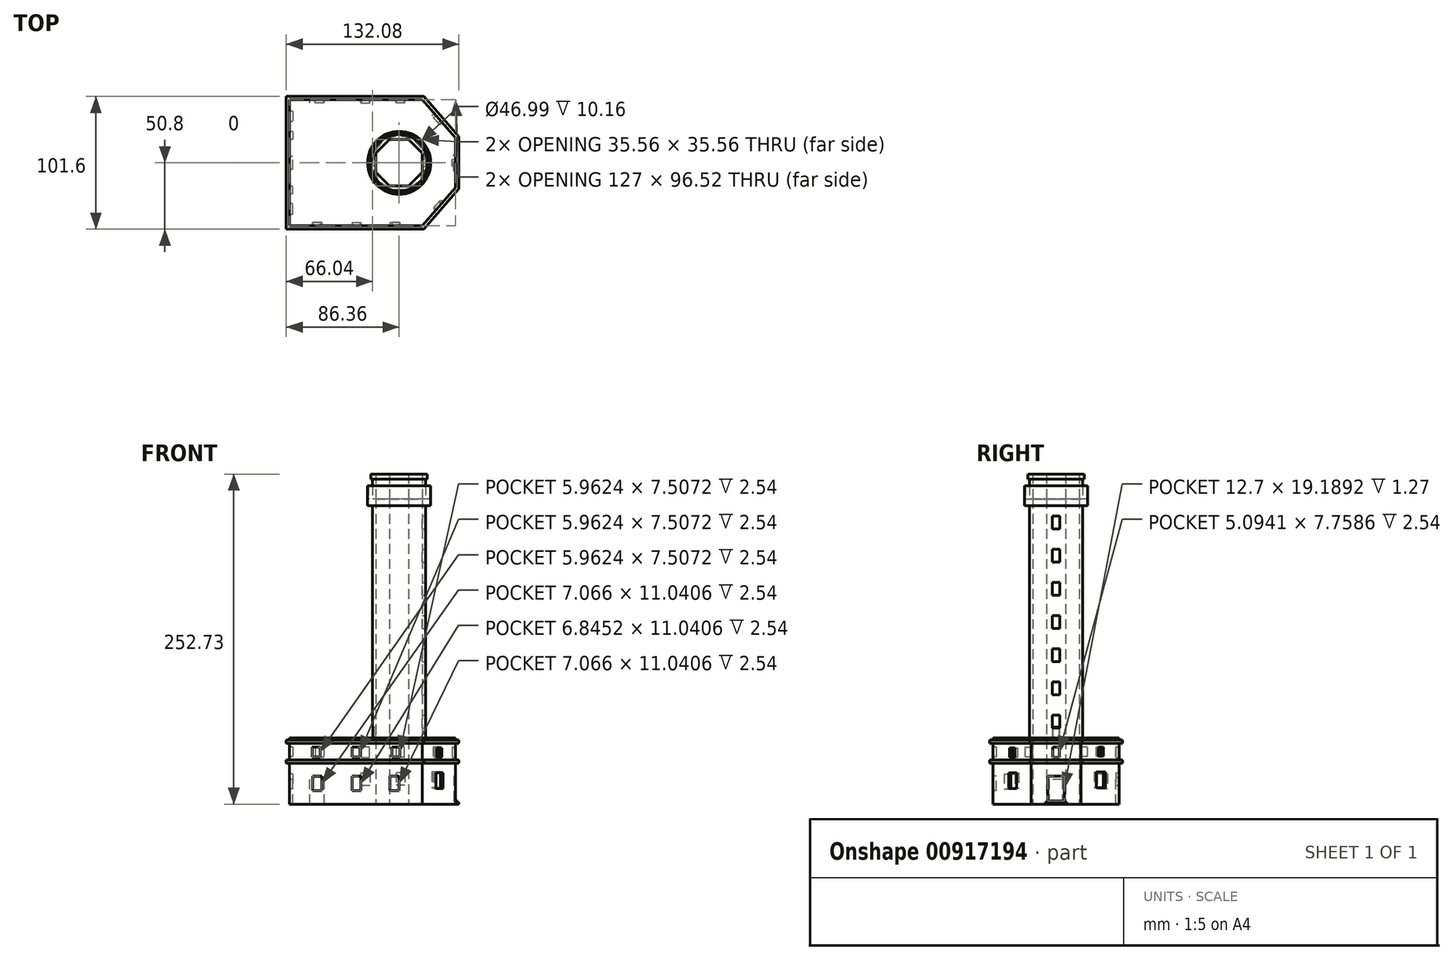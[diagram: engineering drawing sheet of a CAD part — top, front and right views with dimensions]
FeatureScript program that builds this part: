
annotation { "Feature Type Name" : "Feature", "Feature Type Description" : "" }
export const myFeature = defineFeature(function(context is Context, id is Id, definition is map)
    precondition{}
    {
        {
            var Q0;
            Q0=qCreatedBy(makeId("Top.planeOp"),FACE);
            var sketch = newSketch(context, id + "F0", { "sketchPlane" : qUnion([Q0])});
            skLineSegment(sketch, "E0.bottom", {"start": v(50.8, -48.26) * mm, "end": v(-50.8, -48.26) * mm});
            skLineSegment(sketch, "E0.top", {"start": v(50.8, 48.26) * mm, "end": v(-50.8, 48.26) * mm});
            skLineSegment(sketch, "E0.right", {"start": v(-50.8, -48.26) * mm, "end": v(-50.8, 48.26) * mm});
            skPoint(sketch, "E0.middle", {"position": v(0, 0) * mm});
            skLineSegment(sketch, "E1.left", {"start": v(76.2, -19.05) * mm, "end": v(76.2, 19.05) * mm});
            skPoint(sketch, "E1.middle", {"position": v(50.8, 0) * mm});
            skLineSegment(sketch, "E2", {"start": v(50.8, 48.26) * mm, "end": v(76.2, 19.05) * mm});
            skLineSegment(sketch, "E3", {"start": v(50.8, -48.26) * mm, "end": v(76.2, -19.05) * mm});
            skSolve(sketch);
        }
        {
            var Q0;
            Q0=makeQuery(id+"F0.imprint","IMPRINT",FACE,{"disambiguationData":[TD([[makeQuery(id+"F0.imprint","IMPRINT",EDGE,{"derivedFrom":sQuery(id+"F0.wireOp",EDGE,"E0.bottom")}),-1.0]])]});
            extrude(context, id + "F1", {"entities" : qUnion([Q0]), "depth" : 50.8 * mm, "offsetDistance" : 25.4 * mm});
        }
        {
            var Q0;
            Q0=makeQuery(id+"F1.opExtrude","CAP_FACE",FACE,{"disambiguationData":[OSD([sQuery(id+"F0.wireOp",EDGE,"E0.bottom"),sQuery(id+"F0.wireOp",EDGE,"E0.top"),sQuery(id+"F0.wireOp",EDGE,"E0.right"),sQuery(id+"F0.wireOp",EDGE,"E1.left"),sQuery(id+"F0.wireOp",EDGE,"E2"),sQuery(id+"F0.wireOp",EDGE,"E3")])],"isStart":false});
            var sketch = newSketch(context, id + "F2", { "sketchPlane" : qUnion([Q0])});
            skCircle(sketch, "E4", {"center": v(33.02, 0) * mm, "radius": 20.32 * mm});
            skSolve(sketch);
        }
        {
            var Q0;
            Q0=makeQuery(id+"F2.imprint","IMPRINT",FACE,{"disambiguationData":[TD([[makeQuery(id+"F2.imprint","IMPRINT",EDGE,{"derivedFrom":sQuery(id+"F2.wireOp",EDGE,"E4")}),1.0]])]});
            extrude(context, id + "F3", {"entities" : qUnion([Q0]), "operationType" : NewBodyOperationType.ADD, "depth" : 177.8 * mm, "offsetDistance" : 25.4 * mm});
        }
        {
            var Q0;
            Q0=qCreatedBy(makeId("Top.planeOp"),FACE);
            var sketch = newSketch(context, id + "F4", { "sketchPlane" : qUnion([Q0])});
            skCircle(sketch, "E5.0", {"center": v(33.02, 0) * mm, "radius": 20.32 * mm});
            skPoint(sketch, "E6.0.midPoint", {"position": v(45.32, -7.29) * mm});
            skLineSegment(sketch, "E7", {"start": v(33.02, 0) * mm, "end": v(50.8, 0) * mm});
            skCircle(sketch, "E8.cCircle", {"center": v(33.02, 0) * mm, "radius": 17.78 * mm, "construction": true});
            skLineSegment(sketch, "E8.0", {"start": v(50.8, 7.36) * mm, "end": v(50.8, -7.36) * mm});
            skLineSegment(sketch, "E8.1", {"start": v(50.8, -7.36) * mm, "end": v(40.38, -17.78) * mm});
            skLineSegment(sketch, "E8.2", {"start": v(40.38, -17.78) * mm, "end": v(25.66, -17.78) * mm});
            skLineSegment(sketch, "E8.3", {"start": v(25.66, -17.78) * mm, "end": v(15.24, -7.36) * mm});
            skLineSegment(sketch, "E8.4", {"start": v(15.24, -7.36) * mm, "end": v(15.24, 7.36) * mm});
            skLineSegment(sketch, "E8.5", {"start": v(15.24, 7.36) * mm, "end": v(25.66, 17.78) * mm});
            skLineSegment(sketch, "E8.6", {"start": v(25.66, 17.78) * mm, "end": v(40.38, 17.78) * mm});
            skLineSegment(sketch, "E8.7", {"start": v(40.38, 17.78) * mm, "end": v(50.8, 7.36) * mm});
            skPoint(sketch, "E8.0.midPoint", {"position": v(50.8, 0) * mm});
            skSolve(sketch);
        }
        {
            var Q0;
            {var subQ0=sQuery(id+"F4.wireOp",EDGE,"E8.0");var subQ1=makeQuery(id+"F4.imprint","IMPRINT",VERTEX,{"derivedFrom":subQ0});Q0=makeQuery(id+"F4.imprint","IMPRINT",FACE,{"disambiguationData":[TD([[makeQuery(id+"F4.imprint","IMPRINT",EDGE,{"disambiguationData":[TD([[subQ1,1.0]])],"derivedFrom":subQ0}),-1.0]])]});}
            extrude(context, id + "F5", {"entities" : qUnion([Q0]), "operationType" : NewBodyOperationType.REMOVE, "depth" : 381 * mm, "offsetDistance" : 25.4 * mm});
        }
        {
            var Q0;
            Q0=makeQuery(id+"F1.opExtrude","SWEPT_FACE",FACE,{"disambiguationData":[OSD([sQuery(id+"F0.wireOp",EDGE,"E0.top")])]});
            var sketch = newSketch(context, id + "F6", { "sketchPlane" : qUnion([Q0])});
            skLineSegment(sketch, "E9", {"start": v(-50.8, 50.8) * mm, "end": v(-50.8, 49.28) * mm});
            skLineSegment(sketch, "E10.bottom", {"start": v(-50.8, 49.28) * mm, "end": v(50.8, 49.28) * mm});
            skLineSegment(sketch, "E10.top", {"start": v(-50.8, 46.74) * mm, "end": v(50.8, 46.74) * mm});
            skLineSegment(sketch, "E10.left", {"start": v(-50.8, 49.28) * mm, "end": v(-50.8, 46.74) * mm});
            skLineSegment(sketch, "E10.right", {"start": v(50.8, 49.28) * mm, "end": v(50.8, 46.74) * mm});
            skLineSegment(sketch, "E11", {"start": v(-50.8, 46.74) * mm, "end": v(-50.8, 34.04) * mm});
            skLineSegment(sketch, "E12.bottom", {"start": v(-50.8, 34.04) * mm, "end": v(50.8, 34.04) * mm});
            skLineSegment(sketch, "E12.top", {"start": v(-50.8, 31.5) * mm, "end": v(50.8, 31.5) * mm});
            skLineSegment(sketch, "E12.left", {"start": v(-50.8, 34.04) * mm, "end": v(-50.8, 31.5) * mm});
            skLineSegment(sketch, "E12.right", {"start": v(50.8, 34.04) * mm, "end": v(50.8, 31.5) * mm});
            skLineSegment(sketch, "E13", {"start": v(-50.8, 40.39) * mm, "end": v(50.8, 40.39) * mm});
            skLineSegment(sketch, "E14", {"start": v(0, 50.8) * mm, "end": v(0, 31.5) * mm, "construction": true});
            skLineSegment(sketch, "E15.bottom", {"start": v(3.03, 35.7) * mm, "end": v(-3.03, 35.7) * mm});
            skLineSegment(sketch, "E15.top", {"start": v(3.03, 45.07) * mm, "end": v(-3.03, 45.07) * mm});
            skLineSegment(sketch, "E15.left", {"start": v(3.03, 35.7) * mm, "end": v(3.03, 45.07) * mm});
            skLineSegment(sketch, "E15.right", {"start": v(-3.03, 35.7) * mm, "end": v(-3.03, 45.07) * mm});
            skPoint(sketch, "E15.middle", {"position": v(0, 40.39) * mm});
            skLineSegment(sketch, "E16.1.0.0", {"start": v(30.48, 50.8) * mm, "end": v(30.48, 31.5) * mm, "construction": true});
            skLineSegment(sketch, "E16.2.0.0", {"start": v(60.96, 50.8) * mm, "end": v(60.96, 31.5) * mm, "construction": true});
            skLineSegment(sketch, "E16.direction1", {"start": v(0, 31.5) * mm, "end": v(30.48, 31.5) * mm, "construction": true});
            skLineSegment(sketch, "E17.1.0.0", {"start": v(-30.48, 50.8) * mm, "end": v(-30.48, 31.5) * mm, "construction": true});
            skPoint(sketch, "E17.1.0.1", {"position": v(-30.48, 40.39) * mm});
            skLineSegment(sketch, "E17.2.0.0", {"start": v(-60.96, 50.8) * mm, "end": v(-60.96, 31.5) * mm, "construction": true});
            skPoint(sketch, "E17.2.0.1", {"position": v(-60.96, 40.39) * mm});
            skLineSegment(sketch, "E17.direction1", {"start": v(0, 31.5) * mm, "end": v(-30.48, 31.5) * mm, "construction": true});
            skLineSegment(sketch, "E18.bottom", {"start": v(-27.7, 35.38) * mm, "end": v(-33.27, 35.38) * mm});
            skLineSegment(sketch, "E18.top", {"start": v(-27.7, 45.39) * mm, "end": v(-33.27, 45.39) * mm});
            skLineSegment(sketch, "E18.left", {"start": v(-27.7, 35.38) * mm, "end": v(-27.7, 45.39) * mm});
            skLineSegment(sketch, "E18.right", {"start": v(-33.27, 35.38) * mm, "end": v(-33.27, 45.39) * mm});
            skLineSegment(sketch, "E19.MirrorCS", {"start": v(27.7, 35.38) * mm, "end": v(27.7, 45.39) * mm});
            skLineSegment(sketch, "E20.MirrorCS", {"start": v(27.7, 35.38) * mm, "end": v(33.27, 35.38) * mm});
            skLineSegment(sketch, "E21.MirrorCS", {"start": v(33.27, 35.38) * mm, "end": v(33.27, 45.39) * mm});
            skLineSegment(sketch, "E22.MirrorCS", {"start": v(27.7, 45.39) * mm, "end": v(33.27, 45.39) * mm});
            skSolve(sketch);
        }
        {
            var Q0;
            Q0=makeQuery(id+"F6.imprint","IMPRINT",FACE,{"disambiguationData":[TD([[makeQuery(id+"F6.imprint","IMPRINT",EDGE,{"derivedFrom":sQuery(id+"F6.wireOp",EDGE,"E10.bottom")}),-1.0]])]});
            var Q1;
            Q1=makeQuery(id+"F6.imprint","IMPRINT",FACE,{"disambiguationData":[TD([[makeQuery(id+"F6.imprint","IMPRINT",EDGE,{"derivedFrom":sQuery(id+"F6.wireOp",EDGE,"E12.bottom")}),-1.0]])]});
            extrude(context, id + "F7", {"entities" : qUnion([Q0, Q1]), "operationType" : NewBodyOperationType.ADD, "depth" : 2.54 * mm, "offsetDistance" : 25.4 * mm});
        }
        {
            var Q0;
            Q0=makeQuery(id+"F1.opExtrude","SWEPT_FACE",FACE,{"disambiguationData":[OSD([sQuery(id+"F0.wireOp",EDGE,"E2")])]});
            var sketch = newSketch(context, id + "F8", { "sketchPlane" : qUnion([Q0])});
            skLineSegment(sketch, "E23", {"start": v(-35.63, 50.8) * mm, "end": v(-35.63, 49.28) * mm});
            skLineSegment(sketch, "E24.bottom", {"start": v(-35.63, 49.28) * mm, "end": v(3.08, 49.28) * mm});
            skLineSegment(sketch, "E24.top", {"start": v(-35.63, 46.74) * mm, "end": v(3.08, 46.74) * mm});
            skLineSegment(sketch, "E24.left", {"start": v(-35.63, 49.28) * mm, "end": v(-35.63, 46.74) * mm});
            skLineSegment(sketch, "E24.right", {"start": v(3.08, 49.28) * mm, "end": v(3.08, 46.74) * mm});
            skLineSegment(sketch, "E25.bottom", {"start": v(3.08, 34.04) * mm, "end": v(-35.63, 34.04) * mm});
            skLineSegment(sketch, "E25.top", {"start": v(3.08, 31.5) * mm, "end": v(-35.63, 31.5) * mm});
            skLineSegment(sketch, "E25.left", {"start": v(3.08, 34.04) * mm, "end": v(3.08, 31.5) * mm});
            skLineSegment(sketch, "E25.right", {"start": v(-35.63, 34.04) * mm, "end": v(-35.63, 31.5) * mm});
            skSolve(sketch);
        }
        {
            var Q0;
            Q0=makeQuery(id+"F8.imprint","IMPRINT",FACE,{"disambiguationData":[TD([[makeQuery(id+"F8.imprint","IMPRINT",EDGE,{"derivedFrom":sQuery(id+"F8.wireOp",EDGE,"E24.bottom")}),-1.0]])]});
            var Q1;
            Q1=makeQuery(id+"F8.imprint","IMPRINT",FACE,{"disambiguationData":[TD([[makeQuery(id+"F8.imprint","IMPRINT",EDGE,{"derivedFrom":sQuery(id+"F8.wireOp",EDGE,"E25.bottom")}),1.0]])]});
            extrude(context, id + "F9", {"entities" : qUnion([Q0, Q1]), "operationType" : NewBodyOperationType.ADD, "depth" : 2.54 * mm, "offsetDistance" : 25.4 * mm});
        }
        {
            var Q0;
            Q0=makeQuery(id+"F7.opExtrude","SWEPT_FACE",FACE,{"disambiguationData":[OSD([sQuery(id+"F6.wireOp",EDGE,"E10.left")])]});
            extrude(context, id + "F10", {"entities" : qUnion([Q0]), "operationType" : NewBodyOperationType.ADD, "depth" : 1.14 * mm, "offsetDistance" : 25.4 * mm});
        }
        {
            var Q0;
            Q0=makeQuery(id+"F9.opExtrude","SWEPT_FACE",FACE,{"disambiguationData":[OSD([sQuery(id+"F8.wireOp",EDGE,"E24.right")])]});
            extrude(context, id + "F11", {"entities" : qUnion([Q0]), "operationType" : NewBodyOperationType.ADD, "depth" : 1.14 * mm, "offsetDistance" : 25.4 * mm});
        }
        {
            var Q0;
            Q0=makeQuery(id+"F7.opExtrude","SWEPT_FACE",FACE,{"disambiguationData":[OSD([sQuery(id+"F6.wireOp",EDGE,"E12.left")])]});
            extrude(context, id + "F12", {"entities" : qUnion([Q0]), "operationType" : NewBodyOperationType.ADD, "depth" : 1.14 * mm, "offsetDistance" : 25.4 * mm});
        }
        {
            var Q0;
            Q0=makeQuery(id+"F9.opExtrude","SWEPT_FACE",FACE,{"disambiguationData":[OSD([sQuery(id+"F8.wireOp",EDGE,"E25.left")])]});
            extrude(context, id + "F13", {"entities" : qUnion([Q0]), "operationType" : NewBodyOperationType.ADD, "depth" : 1.14 * mm, "offsetDistance" : 25.4 * mm});
        }
        {
            var Q0;
            Q0=makeQuery(id+"F1.opExtrude","SWEPT_FACE",FACE,{"disambiguationData":[OSD([sQuery(id+"F0.wireOp",EDGE,"E1.left")])]});
            var sketch = newSketch(context, id + "F14", { "sketchPlane" : qUnion([Q0])});
            skLineSegment(sketch, "E26.bottom", {"start": v(19.05, 49.28) * mm, "end": v(-19.05, 49.28) * mm});
            skLineSegment(sketch, "E26.top", {"start": v(19.05, 46.74) * mm, "end": v(-19.05, 46.74) * mm});
            skLineSegment(sketch, "E26.left", {"start": v(19.05, 49.28) * mm, "end": v(19.05, 46.74) * mm});
            skLineSegment(sketch, "E26.right", {"start": v(-19.05, 49.28) * mm, "end": v(-19.05, 46.74) * mm});
            skLineSegment(sketch, "E27.bottom", {"start": v(19.05, 34.04) * mm, "end": v(-19.05, 34.04) * mm});
            skLineSegment(sketch, "E27.top", {"start": v(19.05, 31.5) * mm, "end": v(-19.05, 31.5) * mm});
            skLineSegment(sketch, "E27.left", {"start": v(19.05, 34.04) * mm, "end": v(19.05, 31.5) * mm});
            skLineSegment(sketch, "E27.right", {"start": v(-19.05, 34.04) * mm, "end": v(-19.05, 31.5) * mm});
            skPoint(sketch, "E28.top.end.orphan", {"position": v(6.35, 21.6) * mm});
            skPoint(sketch, "E28.top.start.orphan", {"position": v(0, 21.6) * mm});
            skPoint(sketch, "E29.MirrorCS.end.orphan", {"position": v(-6.35, 21.6) * mm});
            skPoint(sketch, "E30.MirrorCS.end.orphan", {"position": v(-6.35, 21.59) * mm});
            skPoint(sketch, "E30.MirrorCS.start.orphan", {"position": v(-6.35, 0) * mm});
            skPoint(sketch, "E28.bottom.end.orphan", {"position": v(6.35, 0) * mm});
            skPoint(sketch, "E28.bottom.start.orphan", {"position": v(0, 0) * mm});
            skSolve(sketch);
        }
        {
            var Q0;
            Q0=makeQuery(id+"F14.imprint","IMPRINT",FACE,{"disambiguationData":[TD([[makeQuery(id+"F14.imprint","IMPRINT",EDGE,{"derivedFrom":sQuery(id+"F14.wireOp",EDGE,"E26.bottom")}),1.0]])]});
            var Q1;
            Q1=makeQuery(id+"F14.imprint","IMPRINT",FACE,{"disambiguationData":[TD([[makeQuery(id+"F14.imprint","IMPRINT",EDGE,{"derivedFrom":sQuery(id+"F14.wireOp",EDGE,"E27.bottom")}),1.0]])]});
            extrude(context, id + "F15", {"entities" : qUnion([Q0, Q1]), "operationType" : NewBodyOperationType.ADD, "depth" : 2.54 * mm, "offsetDistance" : 25.4 * mm});
        }
        {
            var Q0;
            Q0=makeQuery(id+"F15.opExtrude","SWEPT_FACE",FACE,{"disambiguationData":[OSD([sQuery(id+"F14.wireOp",EDGE,"E26.left")])]});
            var Q1;
            Q1=makeQuery(id+"F15.opExtrude","SWEPT_FACE",FACE,{"disambiguationData":[OSD([sQuery(id+"F14.wireOp",EDGE,"E27.left")])]});
            extrude(context, id + "F16", {"entities" : qUnion([Q0, Q1]), "operationType" : NewBodyOperationType.ADD, "depth" : 0.89 * mm, "offsetDistance" : 25.4 * mm});
        }
        {
            var Q0;
            Q0=makeQuery(id+"F9.opExtrude","SWEPT_FACE",FACE,{"disambiguationData":[OSD([sQuery(id+"F8.wireOp",EDGE,"E24.left")])]});
            var Q1;
            Q1=makeQuery(id+"F9.opExtrude","SWEPT_FACE",FACE,{"disambiguationData":[OSD([sQuery(id+"F8.wireOp",EDGE,"E25.right")])]});
            extrude(context, id + "F17", {"entities" : qUnion([Q0, Q1]), "operationType" : NewBodyOperationType.ADD, "depth" : 0.89 * mm, "offsetDistance" : 25.4 * mm});
        }
        {
            var Q0;
            Q0=makeQuery(id+"F1.opExtrude","SWEPT_FACE",FACE,{"disambiguationData":[OSD([sQuery(id+"F0.wireOp",EDGE,"E3")])]});
            var sketch = newSketch(context, id + "F18", { "sketchPlane" : qUnion([Q0])});
            skLineSegment(sketch, "E31.bottom", {"start": v(35.63, 49.28) * mm, "end": v(-3.08, 49.28) * mm});
            skLineSegment(sketch, "E31.top", {"start": v(35.63, 46.74) * mm, "end": v(-3.08, 46.74) * mm});
            skLineSegment(sketch, "E31.left", {"start": v(35.63, 49.28) * mm, "end": v(35.63, 46.74) * mm});
            skLineSegment(sketch, "E31.right", {"start": v(-3.08, 49.28) * mm, "end": v(-3.08, 46.74) * mm});
            skLineSegment(sketch, "E32.bottom", {"start": v(35.63, 34.04) * mm, "end": v(-3.08, 34.04) * mm});
            skLineSegment(sketch, "E32.top", {"start": v(35.63, 31.5) * mm, "end": v(-3.08, 31.5) * mm});
            skLineSegment(sketch, "E32.left", {"start": v(35.63, 34.04) * mm, "end": v(35.63, 31.5) * mm});
            skLineSegment(sketch, "E32.right", {"start": v(-3.08, 34.04) * mm, "end": v(-3.08, 31.5) * mm});
            skSolve(sketch);
        }
        {
            var Q0;
            Q0=makeQuery(id+"F18.imprint","IMPRINT",FACE,{"disambiguationData":[TD([[makeQuery(id+"F18.imprint","IMPRINT",EDGE,{"derivedFrom":sQuery(id+"F18.wireOp",EDGE,"E31.bottom")}),1.0]])]});
            var Q1;
            Q1=makeQuery(id+"F18.imprint","IMPRINT",FACE,{"disambiguationData":[TD([[makeQuery(id+"F18.imprint","IMPRINT",EDGE,{"derivedFrom":sQuery(id+"F18.wireOp",EDGE,"E32.bottom")}),1.0]])]});
            extrude(context, id + "F19", {"entities" : qUnion([Q0, Q1]), "operationType" : NewBodyOperationType.ADD, "depth" : 2.54 * mm, "offsetDistance" : 25.4 * mm});
        }
        {
            var Q0;
            Q0=makeQuery(id+"F1.opExtrude","SWEPT_FACE",FACE,{"disambiguationData":[OSD([sQuery(id+"F0.wireOp",EDGE,"E0.bottom")])]});
            var sketch = newSketch(context, id + "F20", { "sketchPlane" : qUnion([Q0])});
            skLineSegment(sketch, "E33.bottom", {"start": v(50.8, 49.28) * mm, "end": v(-50.8, 49.28) * mm});
            skLineSegment(sketch, "E33.top", {"start": v(50.8, 46.74) * mm, "end": v(-50.8, 46.74) * mm});
            skLineSegment(sketch, "E33.left", {"start": v(50.8, 49.28) * mm, "end": v(50.8, 46.74) * mm});
            skLineSegment(sketch, "E33.right", {"start": v(-50.8, 49.28) * mm, "end": v(-50.8, 46.74) * mm});
            skLineSegment(sketch, "E34.bottom", {"start": v(50.8, 34.04) * mm, "end": v(-50.8, 34.04) * mm});
            skLineSegment(sketch, "E34.top", {"start": v(50.8, 31.5) * mm, "end": v(-50.8, 31.5) * mm});
            skLineSegment(sketch, "E34.left", {"start": v(50.8, 34.04) * mm, "end": v(50.8, 31.5) * mm});
            skLineSegment(sketch, "E34.right", {"start": v(-50.8, 34.04) * mm, "end": v(-50.8, 31.5) * mm});
            skSolve(sketch);
        }
        {
            var Q0;
            Q0 = qSketchRegion(id + "F20", true);
            extrude(context, id + "F21", {"entities" : qUnion([Q0]), "operationType" : NewBodyOperationType.ADD, "depth" : 2.54 * mm, "offsetDistance" : 25.4 * mm});
        }
        {
            var Q0;
            Q0=makeQuery(id+"F15.opExtrude","SWEPT_FACE",FACE,{"disambiguationData":[OSD([sQuery(id+"F14.wireOp",EDGE,"E26.right")])]});
            var Q1;
            Q1=makeQuery(id+"F15.opExtrude","SWEPT_FACE",FACE,{"disambiguationData":[OSD([sQuery(id+"F14.wireOp",EDGE,"E27.right")])]});
            extrude(context, id + "F22", {"entities" : qUnion([Q0, Q1]), "operationType" : NewBodyOperationType.ADD, "depth" : 0.89 * mm, "offsetDistance" : 25.4 * mm});
        }
        {
            var Q0;
            Q0=makeQuery(id+"F19.opExtrude","SWEPT_FACE",FACE,{"disambiguationData":[OSD([sQuery(id+"F18.wireOp",EDGE,"E31.left")])]});
            var Q1;
            Q1=makeQuery(id+"F19.opExtrude","SWEPT_FACE",FACE,{"disambiguationData":[OSD([sQuery(id+"F18.wireOp",EDGE,"E32.left")])]});
            extrude(context, id + "F23", {"entities" : qUnion([Q0, Q1]), "operationType" : NewBodyOperationType.ADD, "depth" : 0.89 * mm, "offsetDistance" : 25.4 * mm});
        }
        {
            var Q0;
            Q0=makeQuery(id+"F19.opExtrude","SWEPT_FACE",FACE,{"disambiguationData":[OSD([sQuery(id+"F18.wireOp",EDGE,"E31.right")])]});
            var Q1;
            Q1=makeQuery(id+"F19.opExtrude","SWEPT_FACE",FACE,{"disambiguationData":[OSD([sQuery(id+"F18.wireOp",EDGE,"E32.right")])]});
            extrude(context, id + "F24", {"entities" : qUnion([Q0, Q1]), "operationType" : NewBodyOperationType.ADD, "depth" : 1.14 * mm, "offsetDistance" : 25.4 * mm});
        }
        {
            var Q0;
            Q0=makeQuery(id+"F21.opExtrude","SWEPT_FACE",FACE,{"disambiguationData":[OSD([sQuery(id+"F20.wireOp",EDGE,"E33.left")])]});
            var Q1;
            Q1=makeQuery(id+"F21.opExtrude","SWEPT_FACE",FACE,{"disambiguationData":[OSD([sQuery(id+"F20.wireOp",EDGE,"E34.left")])]});
            extrude(context, id + "F25", {"entities" : qUnion([Q0, Q1]), "operationType" : NewBodyOperationType.ADD, "depth" : 1.14 * mm, "offsetDistance" : 25.4 * mm});
        }
        {
            var Q0;
            Q0=makeQuery(id+"F21.boolean.opBoolean","MERGE",FACE,{"derivedFrom":[makeQuery(id+"F7.boolean.opBoolean","MERGE",FACE,{"derivedFrom":[makeQuery(id+"F1.opExtrude","SWEPT_FACE",FACE,{"disambiguationData":[OSD([sQuery(id+"F0.wireOp",EDGE,"E0.right")])]}),makeQuery(id+"F7.opExtrude","SWEPT_FACE",FACE,{"disambiguationData":[OSD([sQuery(id+"F6.wireOp",EDGE,"E10.right")])]}),makeQuery(id+"F7.opExtrude","SWEPT_FACE",FACE,{"disambiguationData":[OSD([sQuery(id+"F6.wireOp",EDGE,"E12.right")])]})]}),makeQuery(id+"F21.opExtrude","SWEPT_FACE",FACE,{"disambiguationData":[OSD([sQuery(id+"F20.wireOp",EDGE,"E33.right")])]}),makeQuery(id+"F21.opExtrude","SWEPT_FACE",FACE,{"disambiguationData":[OSD([sQuery(id+"F20.wireOp",EDGE,"E34.right")])]})]});
            var sketch = newSketch(context, id + "F26", { "sketchPlane" : qUnion([Q0])});
            skLineSegment(sketch, "E35.bottom", {"start": v(-50.8, 49.28) * mm, "end": v(50.8, 49.28) * mm});
            skLineSegment(sketch, "E35.top", {"start": v(-50.8, 46.74) * mm, "end": v(50.8, 46.74) * mm});
            skLineSegment(sketch, "E35.left", {"start": v(-50.8, 49.28) * mm, "end": v(-50.8, 46.74) * mm});
            skLineSegment(sketch, "E35.right", {"start": v(50.8, 49.28) * mm, "end": v(50.8, 46.74) * mm});
            skLineSegment(sketch, "E36.bottom", {"start": v(-50.8, 34.04) * mm, "end": v(50.8, 34.04) * mm});
            skLineSegment(sketch, "E36.top", {"start": v(-50.8, 31.5) * mm, "end": v(50.8, 31.5) * mm});
            skLineSegment(sketch, "E36.left", {"start": v(-50.8, 34.04) * mm, "end": v(-50.8, 31.5) * mm});
            skLineSegment(sketch, "E36.right", {"start": v(50.8, 34.04) * mm, "end": v(50.8, 31.5) * mm});
            skSolve(sketch);
        }
        {
            var Q0;
            {var subQ15=sQuery(id+"F26.wireOp",EDGE,"E35.left");Q0=makeQuery(id+"F26.imprint","IMPRINT",FACE,{"disambiguationData":[TD([[makeQuery(id+"F26.imprint","IMPRINT",EDGE,{"derivedFrom":subQ15}),1.0]])]});}
            var Q1;
            {var subQ16=sQuery(id+"F26.wireOp",EDGE,"E36.left");Q1=makeQuery(id+"F26.imprint","IMPRINT",FACE,{"disambiguationData":[TD([[makeQuery(id+"F26.imprint","IMPRINT",EDGE,{"derivedFrom":subQ16}),1.0]])]});}
            extrude(context, id + "F27", {"entities" : qUnion([Q0, Q1]), "operationType" : NewBodyOperationType.ADD, "depth" : 2.54 * mm, "offsetDistance" : 25.4 * mm});
        }
        {
            var Q0;
            {var subQ0=sQuery(id+"F6.wireOp",EDGE,"E12.top");var subQ5=sQuery(id+"F0.wireOp",EDGE,"E1.left");Q0=makeQuery(id+"F15.boolean.opBoolean","SPLIT",FACE,{"disambiguationData":[TD([makeQuery(id+"F7.opExtrude","SWEPT_FACE",FACE,{"disambiguationData":[OSD([subQ0])]})])],"derivedFrom":makeQuery(id+"F1.opExtrude","SWEPT_FACE",FACE,{"disambiguationData":[OSD([subQ5])]})});}
            var sketch = newSketch(context, id + "F28", { "sketchPlane" : qUnion([Q0])});
            skLineSegment(sketch, "E37.bottom", {"start": v(0, 0) * mm, "end": v(6.35, 0) * mm});
            skLineSegment(sketch, "E37.top", {"start": v(0, 21.6) * mm, "end": v(6.35, 21.6) * mm});
            skLineSegment(sketch, "E38.MirrorCS", {"start": v(0, 21.6) * mm, "end": v(-6.35, 21.6) * mm});
            skLineSegment(sketch, "E39.top", {"start": v(-6.35, 1.4) * mm, "end": v(6.35, 1.4) * mm});
            skLineSegment(sketch, "E39.left", {"start": v(-6.35, 21.6) * mm, "end": v(-6.35, 2.4) * mm});
            skLineSegment(sketch, "E39.right", {"start": v(6.35, 21.6) * mm, "end": v(6.35, 2.4) * mm});
            skLineSegment(sketch, "E40", {"start": v(6.35, 1.4) * mm, "end": v(8.38, 1.4) * mm});
            skLineSegment(sketch, "E41", {"start": v(8.38, 1.4) * mm, "end": v(8.38, 0) * mm});
            skLineSegment(sketch, "E42", {"start": v(-8.8, 0) * mm, "end": v(8.38, 0) * mm});
            skLineSegment(sketch, "E43.MirrorCS", {"start": v(-6.35, 1.4) * mm, "end": v(-8.38, 1.4) * mm});
            skLineSegment(sketch, "E44.MirrorCS", {"start": v(-8.38, 1.4) * mm, "end": v(-8.38, 0) * mm});
            skLineSegment(sketch, "E45", {"start": v(-8.38, 0) * mm, "end": v(8.38, 0) * mm});
            skLineSegment(sketch, "E46", {"start": v(-7.37, 1.4) * mm, "end": v(-7.37, 2.4) * mm});
            skLineSegment(sketch, "E47", {"start": v(-7.37, 2.4) * mm, "end": v(7.37, 2.4) * mm});
            skPoint(sketch, "E47.endSnap0", {"position": v(7.37, 1.4) * mm});
            skLineSegment(sketch, "E48", {"start": v(7.37, 2.4) * mm, "end": v(7.37, 1.4) * mm});
            skLineSegment(sketch, "E49.bottom", {"start": v(-2.55, 43.67) * mm, "end": v(2.55, 43.67) * mm});
            skLineSegment(sketch, "E49.top", {"start": v(-2.55, 35.9) * mm, "end": v(2.55, 35.9) * mm});
            skLineSegment(sketch, "E49.left", {"start": v(-2.55, 43.67) * mm, "end": v(-2.55, 35.9) * mm});
            skLineSegment(sketch, "E49.right", {"start": v(2.55, 43.67) * mm, "end": v(2.55, 35.9) * mm});
            skSolve(sketch);
        }
        {
            var Q0;
            Q0=makeQuery(id+"F28.imprint","IMPRINT",FACE,{"disambiguationData":[TD([[makeQuery(id+"F28.imprint","IMPRINT",EDGE,{"derivedFrom":sQuery(id+"F28.wireOp",EDGE,"E37.top")}),-1.0]])]});
            extrude(context, id + "F29", {"entities" : qUnion([Q0]), "operationType" : NewBodyOperationType.REMOVE, "oppositeDirection" : true, "depth" : 1.27 * mm, "offsetDistance" : 25.4 * mm});
        }
        {
            var Q0;
            {var subQ1=sQuery(id+"F28.wireOp",EDGE,"E39.top");Q0=makeQuery(id+"F28.imprint","IMPRINT",FACE,{"disambiguationData":[TD([[makeQuery(id+"F28.imprint","IMPRINT",EDGE,{"derivedFrom":subQ1}),1.0]])]});}
            extrude(context, id + "F30", {"entities" : qUnion([Q0]), "operationType" : NewBodyOperationType.ADD, "depth" : 1.52 * mm, "offsetDistance" : 25.4 * mm});
        }
        {
            var Q0;
            {var subQ3=sQuery(id+"F28.wireOp",EDGE,"E39.top");Q0=makeQuery(id+"F28.imprint","IMPRINT",FACE,{"disambiguationData":[TD([[makeQuery(id+"F28.imprint","IMPRINT",EDGE,{"derivedFrom":subQ3}),-1.0]])]});}
            extrude(context, id + "F31", {"entities" : qUnion([Q0]), "operationType" : NewBodyOperationType.ADD, "depth" : 2.54 * mm, "offsetDistance" : 25.4 * mm});
        }
        {
            var Q0;
            Q0=makeQuery(id+"F28.imprint","IMPRINT",FACE,{"disambiguationData":[TD([[makeQuery(id+"F28.imprint","IMPRINT",EDGE,{"derivedFrom":sQuery(id+"F28.wireOp",EDGE,"E49.bottom")}),-1.0]])]});
            extrude(context, id + "F32", {"entities" : qUnion([Q0]), "operationType" : NewBodyOperationType.REMOVE, "oppositeDirection" : true, "depth" : 2.54 * mm, "offsetDistance" : 25.4 * mm});
        }
        {
            var Q0;
            Q0=makeQuery(id+"F3.opExtrude","CAP_FACE",FACE,{"disambiguationData":[OSD([sQuery(id+"F2.wireOp",EDGE,"E4")])],"isStart":false});
            var sketch = newSketch(context, id + "F33", { "sketchPlane" : qUnion([Q0])});
            skLineSegment(sketch, "E50", {"start": v(0, 0) * mm, "end": v(53.34, 0) * mm, "construction": true});
            skCircle(sketch, "E51", {"center": v(33.02, 0) * mm, "radius": 24.13 * mm});
            skSolve(sketch);
        }
        {
            var Q0;
            Q0=makeQuery(id+"F33.imprint","IMPRINT",FACE,{"disambiguationData":[TD([[makeQuery(id+"F33.imprint","IMPRINT",EDGE,{"derivedFrom":sQuery(id+"F33.wireOp",EDGE,"E51")}),1.0]])]});
            var Q1;
            {var subQ0=sQuery(id+"F2.wireOp",EDGE,"E4");Q1=makeQuery(id+"F33.imprint","IMPRINT",FACE,{"disambiguationData":[TD([[makeQuery(id+"F33.imprint","IMPRINT",EDGE,{"derivedFrom":makeQuery(id+"F3.opExtrude","CAP_EDGE",EDGE,{"disambiguationData":[OSD([subQ0])],"isStart":false})}),1.0]])]});}
            extrude(context, id + "F34", {"entities" : qUnion([Q0, Q1]), "operationType" : NewBodyOperationType.ADD, "depth" : 5.08 * mm, "offsetDistance" : 25.4 * mm});
        }
        {
            var Q0;
            Q0=makeQuery(id+"F34.opExtrude","CAP_FACE",FACE,{"disambiguationData":[OSD([sQuery(id+"F2.wireOp",EDGE,"E4"),sQuery(id+"F4.wireOp",EDGE,"E8.0"),sQuery(id+"F4.wireOp",EDGE,"E8.1"),sQuery(id+"F4.wireOp",EDGE,"E8.2"),sQuery(id+"F4.wireOp",EDGE,"E8.3"),sQuery(id+"F4.wireOp",EDGE,"E8.4"),sQuery(id+"F4.wireOp",EDGE,"E8.5"),sQuery(id+"F4.wireOp",EDGE,"E8.6"),sQuery(id+"F4.wireOp",EDGE,"E8.7"),sQuery(id+"F33.wireOp",EDGE,"E51")])],"isStart":false});
            var sketch = newSketch(context, id + "F35", { "sketchPlane" : qUnion([Q0])});
            skCircle(sketch, "E52", {"center": v(33.02, 0) * mm, "radius": 20.32 * mm});
            skCircle(sketch, "E53", {"center": v(33.02, 0) * mm, "radius": 22.6 * mm});
            skSolve(sketch);
        }
        {
            var Q0;
            Q0=makeQuery(id+"F35.imprint","IMPRINT",FACE,{"disambiguationData":[TD([[makeQuery(id+"F35.imprint","IMPRINT",EDGE,{"derivedFrom":sQuery(id+"F35.wireOp",EDGE,"E52")}),1.0]])]});
            extrude(context, id + "F36", {"entities" : qUnion([Q0]), "depth" : 15.24 * mm, "offsetDistance" : 25.4 * mm});
        }
        {
            var Q0;
            Q0=makeQuery(id+"F36.opExtrude","CAP_FACE",FACE,{"disambiguationData":[OSD([sQuery(id+"F2.wireOp",EDGE,"E4"),sQuery(id+"F4.wireOp",EDGE,"E8.0"),sQuery(id+"F4.wireOp",EDGE,"E8.1"),sQuery(id+"F4.wireOp",EDGE,"E8.2"),sQuery(id+"F4.wireOp",EDGE,"E8.3"),sQuery(id+"F4.wireOp",EDGE,"E8.4"),sQuery(id+"F4.wireOp",EDGE,"E8.5"),sQuery(id+"F4.wireOp",EDGE,"E8.6"),sQuery(id+"F4.wireOp",EDGE,"E8.7"),sQuery(id+"F35.wireOp",EDGE,"E52")])],"isStart":false});
            var sketch = newSketch(context, id + "F37", { "sketchPlane" : qUnion([Q0])});
            skCircle(sketch, "E54", {"center": v(33.02, 0) * mm, "radius": 21.59 * mm});
            skSolve(sketch);
        }
        {
            var Q0;
            Q0=makeQuery(id+"F37.imprint","IMPRINT",FACE,{"disambiguationData":[TD([[makeQuery(id+"F37.imprint","IMPRINT",EDGE,{"derivedFrom":makeQuery(id+"F36.opExtrude","CAP_EDGE",EDGE,{"disambiguationData":[OSD([sQuery(id+"F35.wireOp",EDGE,"E52")])],"isStart":false})}),1.0]])]});
            var Q1;
            Q1=makeQuery(id+"F37.imprint","IMPRINT",FACE,{"disambiguationData":[TD([[makeQuery(id+"F37.imprint","IMPRINT",EDGE,{"derivedFrom":sQuery(id+"F37.wireOp",EDGE,"E54")}),1.0]])]});
            extrude(context, id + "F38", {"entities" : qUnion([Q0, Q1]), "operationType" : NewBodyOperationType.ADD, "depth" : 3.8 * mm, "offsetDistance" : 25.4 * mm});
        }
        {
            var Q0;
            Q0=makeQuery(id+"F34.opExtrude","CAP_FACE",FACE,{"disambiguationData":[OSD([sQuery(id+"F2.wireOp",EDGE,"E4"),sQuery(id+"F4.wireOp",EDGE,"E8.0"),sQuery(id+"F4.wireOp",EDGE,"E8.1"),sQuery(id+"F4.wireOp",EDGE,"E8.2"),sQuery(id+"F4.wireOp",EDGE,"E8.3"),sQuery(id+"F4.wireOp",EDGE,"E8.4"),sQuery(id+"F4.wireOp",EDGE,"E8.5"),sQuery(id+"F4.wireOp",EDGE,"E8.6"),sQuery(id+"F4.wireOp",EDGE,"E8.7"),sQuery(id+"F33.wireOp",EDGE,"E51")])],"isStart":false});
            var sketch = newSketch(context, id + "F39", { "sketchPlane" : qUnion([Q0])});
            skCircle(sketch, "E55", {"center": v(33.02, 0) * mm, "radius": 23.5 * mm});
            skSolve(sketch);
        }
        {
            var Q0;
            Q0=makeQuery(id+"F39.imprint","IMPRINT",FACE,{"disambiguationData":[TD([[makeQuery(id+"F39.imprint","IMPRINT",EDGE,{"derivedFrom":sQuery(id+"F39.wireOp",EDGE,"E55")}),-1.0]])]});
            extrude(context, id + "F40", {"entities" : qUnion([Q0]), "operationType" : NewBodyOperationType.ADD, "depth" : 10.16 * mm, "offsetDistance" : 25.4 * mm});
        }
        {
            var Q0;
            {var subQ2=sQuery(id+"F0.wireOp",EDGE,"E0.top");Q0=makeQuery(id+"F7.boolean.opBoolean","SPLIT",FACE,{"disambiguationData":[TD([makeQuery(id+"F7.opExtrude","SWEPT_FACE",FACE,{"disambiguationData":[OSD([sQuery(id+"F6.wireOp",EDGE,"E12.top")])]})])],"derivedFrom":makeQuery(id+"F1.opExtrude","SWEPT_FACE",FACE,{"disambiguationData":[OSD([subQ2])]})});}
            var sketch = newSketch(context, id + "F41", { "sketchPlane" : qUnion([Q0])});
            skLineSegment(sketch, "E56.bottom", {"start": v(24.22, 0) * mm, "end": v(35.25, 0) * mm});
            skLineSegment(sketch, "E56.top", {"start": v(24.22, 20.73) * mm, "end": v(35.25, 20.73) * mm});
            skLineSegment(sketch, "E56.left", {"start": v(24.22, 0) * mm, "end": v(24.22, 20.73) * mm});
            skLineSegment(sketch, "E56.right", {"start": v(35.25, 0) * mm, "end": v(35.25, 20.73) * mm});
            skLineSegment(sketch, "E57.bottom", {"start": v(-37.5, 24.15) * mm, "end": v(-30.66, 24.15) * mm});
            skLineSegment(sketch, "E57.top", {"start": v(-37.5, 14.43) * mm, "end": v(-30.66, 14.43) * mm});
            skLineSegment(sketch, "E57.left", {"start": v(-37.5, 24.15) * mm, "end": v(-37.5, 14.43) * mm});
            skLineSegment(sketch, "E57.right", {"start": v(-30.66, 24.15) * mm, "end": v(-30.66, 14.43) * mm});
            skLineSegment(sketch, "E58", {"start": v(-20.69, 31.5) * mm, "end": v(-20.69, 0) * mm, "construction": true});
            skLineSegment(sketch, "E59.MirrorCS", {"start": v(-3.88, 24.15) * mm, "end": v(-10.7, 24.15) * mm});
            skLineSegment(sketch, "E60.MirrorCS", {"start": v(-10.7, 24.15) * mm, "end": v(-10.7, 14.43) * mm});
            skLineSegment(sketch, "E61.MirrorCS", {"start": v(-3.88, 14.43) * mm, "end": v(-10.7, 14.43) * mm});
            skLineSegment(sketch, "E62.MirrorCS", {"start": v(-3.88, 24.15) * mm, "end": v(-3.88, 14.43) * mm});
            skPoint(sketch, "E63.end.orphan", {"position": v(-17, 0) * mm});
            skLineSegment(sketch, "E64.bottom", {"start": v(-36.97, 35.96) * mm, "end": v(-30.93, 35.96) * mm});
            skLineSegment(sketch, "E64.top", {"start": v(-36.97, 44.1) * mm, "end": v(-30.93, 44.1) * mm});
            skLineSegment(sketch, "E64.left", {"start": v(-36.97, 35.96) * mm, "end": v(-36.97, 44.1) * mm});
            skLineSegment(sketch, "E64.right", {"start": v(-30.93, 35.96) * mm, "end": v(-30.93, 44.1) * mm});
            skLineSegment(sketch, "E65.MirrorCS", {"start": v(-4.4, 44.1) * mm, "end": v(-10.45, 44.1) * mm});
            skLineSegment(sketch, "E66.MirrorCS", {"start": v(-10.45, 35.96) * mm, "end": v(-10.45, 44.1) * mm});
            skLineSegment(sketch, "E67.MirrorCS", {"start": v(-4.4, 35.96) * mm, "end": v(-10.45, 35.96) * mm});
            skLineSegment(sketch, "E68.MirrorCS", {"start": v(-4.4, 35.96) * mm, "end": v(-4.4, 44.1) * mm});
            skLineSegment(sketch, "E69.bottom", {"start": v(24.48, 43.84) * mm, "end": v(31.3, 43.84) * mm});
            skLineSegment(sketch, "E69.top", {"start": v(24.48, 35.7) * mm, "end": v(31.3, 35.7) * mm});
            skLineSegment(sketch, "E69.left", {"start": v(24.48, 43.84) * mm, "end": v(24.48, 35.7) * mm});
            skLineSegment(sketch, "E69.right", {"start": v(31.3, 43.84) * mm, "end": v(31.3, 35.7) * mm});
            skSolve(sketch);
        }
        {
            var Q0;
            Q0=makeQuery(id+"F41.imprint","IMPRINT",FACE,{"disambiguationData":[TD([[makeQuery(id+"F41.imprint","IMPRINT",EDGE,{"derivedFrom":sQuery(id+"F41.wireOp",EDGE,"E57.bottom")}),-1.0]])]});
            var Q1;
            Q1=makeQuery(id+"F41.imprint","IMPRINT",FACE,{"disambiguationData":[TD([[makeQuery(id+"F41.imprint","IMPRINT",EDGE,{"derivedFrom":sQuery(id+"F41.wireOp",EDGE,"E59.MirrorCS")}),1.0]])]});
            var Q2;
            Q2=makeQuery(id+"F41.imprint","IMPRINT",FACE,{"disambiguationData":[TD([[makeQuery(id+"F41.imprint","IMPRINT",EDGE,{"derivedFrom":sQuery(id+"F41.wireOp",EDGE,"E56.bottom")}),1.0]])]});
            var Q3;
            Q3=makeQuery(id+"F41.imprint","IMPRINT",FACE,{"disambiguationData":[TD([[makeQuery(id+"F41.imprint","IMPRINT",EDGE,{"derivedFrom":sQuery(id+"F41.wireOp",EDGE,"E69.bottom")}),-1.0]])]});
            var Q4;
            Q4=makeQuery(id+"F41.imprint","IMPRINT",FACE,{"disambiguationData":[TD([[makeQuery(id+"F41.imprint","IMPRINT",EDGE,{"derivedFrom":sQuery(id+"F41.wireOp",EDGE,"E65.MirrorCS")}),1.0]])]});
            var Q5;
            Q5=makeQuery(id+"F41.imprint","IMPRINT",FACE,{"disambiguationData":[TD([[makeQuery(id+"F41.imprint","IMPRINT",EDGE,{"derivedFrom":sQuery(id+"F41.wireOp",EDGE,"E64.bottom")}),1.0]])]});
            extrude(context, id + "F42", {"entities" : qUnion([Q0, Q1, Q2, Q3, Q4, Q5]), "operationType" : NewBodyOperationType.REMOVE, "oppositeDirection" : true, "depth" : 2.54 * mm, "offsetDistance" : 25.4 * mm});
        }
        {
            var Q0;
            Q0=makeQuery(id+"F21.boolean.opBoolean","SPLIT",FACE,{"disambiguationData":[TD([makeQuery(id+"F19.opExtrude","SWEPT_FACE",FACE,{"disambiguationData":[OSD([sQuery(id+"F18.wireOp",EDGE,"E31.top")])]})])],"derivedFrom":makeQuery(id+"F1.opExtrude","SWEPT_FACE",FACE,{"disambiguationData":[OSD([sQuery(id+"F0.wireOp",EDGE,"E0.bottom")])]})});
            var sketch = newSketch(context, id + "F43", { "sketchPlane" : qUnion([Q0])});
            skLineSegment(sketch, "E70", {"start": v(0, 0) * mm, "end": v(0, 51.24) * mm, "construction": true});
            skPoint(sketch, "E70.endSnap0", {"position": v(0, 34.04) * mm});
            skLineSegment(sketch, "E71.bottom", {"start": v(-3.01, 21.43) * mm, "end": v(3.83, 21.43) * mm});
            skLineSegment(sketch, "E71.top", {"start": v(-3.01, 10.4) * mm, "end": v(3.83, 10.4) * mm});
            skLineSegment(sketch, "E71.left", {"start": v(-3.01, 21.43) * mm, "end": v(-3.01, 10.4) * mm});
            skLineSegment(sketch, "E71.right", {"start": v(3.83, 21.43) * mm, "end": v(3.83, 10.4) * mm});
            skLineSegment(sketch, "E72.left", {"start": v(-25.98, 10.4) * mm, "end": v(-25.98, 21.43) * mm});
            skLineSegment(sketch, "E73.bottom", {"start": v(-25.98, 10.4) * mm, "end": v(-33.04, 10.4) * mm});
            skLineSegment(sketch, "E73.top", {"start": v(-25.98, 21.43) * mm, "end": v(-33.04, 21.43) * mm});
            skLineSegment(sketch, "E73.right", {"start": v(-33.04, 10.4) * mm, "end": v(-33.04, 21.43) * mm});
            skLineSegment(sketch, "E74.MirrorCS", {"start": v(25.98, 10.4) * mm, "end": v(25.98, 21.43) * mm});
            skLineSegment(sketch, "E75.MirrorCS", {"start": v(25.98, 21.43) * mm, "end": v(33.04, 21.43) * mm});
            skLineSegment(sketch, "E76.MirrorCS", {"start": v(33.04, 10.4) * mm, "end": v(33.04, 21.43) * mm});
            skLineSegment(sketch, "E77.MirrorCS", {"start": v(25.98, 10.4) * mm, "end": v(33.04, 10.4) * mm});
            skLineSegment(sketch, "E78.bottom", {"start": v(-3, 43.74) * mm, "end": v(2.95, 43.74) * mm});
            skLineSegment(sketch, "E78.top", {"start": v(-3, 36.23) * mm, "end": v(2.95, 36.23) * mm});
            skLineSegment(sketch, "E78.left", {"start": v(-3, 43.74) * mm, "end": v(-3, 36.23) * mm});
            skLineSegment(sketch, "E78.right", {"start": v(2.95, 43.74) * mm, "end": v(2.95, 36.23) * mm});
            skLineSegment(sketch, "E79.bottom", {"start": v(-33.48, 43.74) * mm, "end": v(-27.52, 43.74) * mm});
            skLineSegment(sketch, "E79.top", {"start": v(-33.48, 36.23) * mm, "end": v(-27.52, 36.23) * mm});
            skLineSegment(sketch, "E79.left", {"start": v(-33.48, 43.74) * mm, "end": v(-33.48, 36.23) * mm});
            skLineSegment(sketch, "E79.right", {"start": v(-27.52, 43.74) * mm, "end": v(-27.52, 36.23) * mm});
            skLineSegment(sketch, "E80.MirrorCS", {"start": v(27.52, 43.74) * mm, "end": v(27.52, 36.23) * mm});
            skLineSegment(sketch, "E81.MirrorCS", {"start": v(33.48, 43.74) * mm, "end": v(27.52, 43.74) * mm});
            skLineSegment(sketch, "E82.MirrorCS", {"start": v(33.48, 43.74) * mm, "end": v(33.48, 36.23) * mm});
            skLineSegment(sketch, "E83.MirrorCS", {"start": v(33.48, 36.23) * mm, "end": v(27.52, 36.23) * mm});
            skSolve(sketch);
        }
        {
            var Q0;
            Q0=makeQuery(id+"F43.imprint","IMPRINT",FACE,{"disambiguationData":[TD([[makeQuery(id+"F43.imprint","IMPRINT",EDGE,{"derivedFrom":sQuery(id+"F43.wireOp",EDGE,"E73.bottom")}),-1.0]])]});
            var Q1;
            Q1=makeQuery(id+"F43.imprint","IMPRINT",FACE,{"disambiguationData":[TD([[makeQuery(id+"F43.imprint","IMPRINT",EDGE,{"derivedFrom":sQuery(id+"F43.wireOp",EDGE,"E71.bottom")}),-1.0]])]});
            var Q2;
            Q2=makeQuery(id+"F43.imprint","IMPRINT",FACE,{"disambiguationData":[TD([[makeQuery(id+"F43.imprint","IMPRINT",EDGE,{"derivedFrom":sQuery(id+"F43.wireOp",EDGE,"E74.MirrorCS")}),-1.0]])]});
            var Q3;
            Q3=makeQuery(id+"F43.imprint","IMPRINT",FACE,{"disambiguationData":[TD([[makeQuery(id+"F43.imprint","IMPRINT",EDGE,{"derivedFrom":sQuery(id+"F43.wireOp",EDGE,"E80.MirrorCS")}),1.0]])]});
            var Q4;
            Q4=makeQuery(id+"F43.imprint","IMPRINT",FACE,{"disambiguationData":[TD([[makeQuery(id+"F43.imprint","IMPRINT",EDGE,{"derivedFrom":sQuery(id+"F43.wireOp",EDGE,"E78.bottom")}),-1.0]])]});
            var Q5;
            Q5=makeQuery(id+"F43.imprint","IMPRINT",FACE,{"disambiguationData":[TD([[makeQuery(id+"F43.imprint","IMPRINT",EDGE,{"derivedFrom":sQuery(id+"F43.wireOp",EDGE,"E79.bottom")}),-1.0]])]});
            extrude(context, id + "F44", {"entities" : qUnion([Q0, Q1, Q2, Q3, Q4, Q5]), "operationType" : NewBodyOperationType.REMOVE, "oppositeDirection" : true, "depth" : 2.54 * mm, "offsetDistance" : 25.4 * mm});
        }
        {
            var Q0;
            {var subQ2=sQuery(id+"F0.wireOp",EDGE,"E2");Q0=makeQuery(id+"F9.boolean.opBoolean","SPLIT",FACE,{"disambiguationData":[TD([makeQuery(id+"F7.opExtrude","SWEPT_FACE",FACE,{"disambiguationData":[OSD([sQuery(id+"F6.wireOp",EDGE,"E12.top")])]})])],"derivedFrom":makeQuery(id+"F1.opExtrude","SWEPT_FACE",FACE,{"disambiguationData":[OSD([subQ2])]})});}
            var sketch = newSketch(context, id + "F45", { "sketchPlane" : qUnion([Q0])});
            skLineSegment(sketch, "E84.bottom", {"start": v(-19.95, 24.57) * mm, "end": v(-10.6, 24.57) * mm});
            skLineSegment(sketch, "E84.top", {"start": v(-19.95, 12.65) * mm, "end": v(-10.6, 12.65) * mm});
            skLineSegment(sketch, "E84.left", {"start": v(-19.95, 24.57) * mm, "end": v(-19.95, 12.65) * mm});
            skLineSegment(sketch, "E84.right", {"start": v(-10.6, 24.57) * mm, "end": v(-10.6, 12.65) * mm});
            skLineSegment(sketch, "E85.bottom", {"start": v(-18, 36.84) * mm, "end": v(-12.96, 36.84) * mm});
            skLineSegment(sketch, "E85.top", {"start": v(-18, 43.7) * mm, "end": v(-12.96, 43.7) * mm});
            skLineSegment(sketch, "E85.left", {"start": v(-18, 36.84) * mm, "end": v(-18, 43.7) * mm});
            skLineSegment(sketch, "E85.right", {"start": v(-12.96, 36.84) * mm, "end": v(-12.96, 43.7) * mm});
            skSolve(sketch);
        }
        {
            var Q0;
            Q0=makeQuery(id+"F45.imprint","IMPRINT",FACE,{"disambiguationData":[TD([[makeQuery(id+"F45.imprint","IMPRINT",EDGE,{"derivedFrom":sQuery(id+"F45.wireOp",EDGE,"E84.bottom")}),-1.0]])]});
            var Q1;
            Q1=makeQuery(id+"F45.imprint","IMPRINT",FACE,{"disambiguationData":[TD([[makeQuery(id+"F45.imprint","IMPRINT",EDGE,{"derivedFrom":sQuery(id+"F45.wireOp",EDGE,"E85.bottom")}),1.0]])]});
            extrude(context, id + "F46", {"entities" : qUnion([Q0, Q1]), "operationType" : NewBodyOperationType.REMOVE, "oppositeDirection" : true, "depth" : 2.54 * mm, "offsetDistance" : 25.4 * mm});
        }
        {
            var Q0;
            {var subQ0=sQuery(id+"F6.wireOp",EDGE,"E12.top");var subQ7=sQuery(id+"F0.wireOp",EDGE,"E3");Q0=makeQuery(id+"F19.boolean.opBoolean","SPLIT",FACE,{"disambiguationData":[TD([makeQuery(id+"F7.opExtrude","SWEPT_FACE",FACE,{"disambiguationData":[OSD([subQ0])]})])],"derivedFrom":makeQuery(id+"F1.opExtrude","SWEPT_FACE",FACE,{"disambiguationData":[OSD([subQ7])]})});}
            var sketch = newSketch(context, id + "F47", { "sketchPlane" : qUnion([Q0])});
            skLineSegment(sketch, "E86.bottom", {"start": v(12.84, 23.98) * mm, "end": v(20.95, 23.98) * mm});
            skLineSegment(sketch, "E86.top", {"start": v(12.84, 11.9) * mm, "end": v(20.95, 11.9) * mm});
            skLineSegment(sketch, "E86.left", {"start": v(12.84, 23.98) * mm, "end": v(12.84, 11.9) * mm});
            skLineSegment(sketch, "E86.right", {"start": v(20.95, 23.98) * mm, "end": v(20.95, 11.9) * mm});
            skLineSegment(sketch, "E87.bottom", {"start": v(13.93, 43.13) * mm, "end": v(19.35, 43.13) * mm});
            skLineSegment(sketch, "E87.top", {"start": v(13.93, 35.82) * mm, "end": v(19.35, 35.82) * mm});
            skLineSegment(sketch, "E87.left", {"start": v(13.93, 43.13) * mm, "end": v(13.93, 35.82) * mm});
            skLineSegment(sketch, "E87.right", {"start": v(19.35, 43.13) * mm, "end": v(19.35, 35.82) * mm});
            skSolve(sketch);
        }
        {
            var Q0;
            Q0=makeQuery(id+"F47.imprint","IMPRINT",FACE,{"disambiguationData":[TD([[makeQuery(id+"F47.imprint","IMPRINT",EDGE,{"derivedFrom":sQuery(id+"F47.wireOp",EDGE,"E86.bottom")}),-1.0]])]});
            var Q1;
            Q1=makeQuery(id+"F47.imprint","IMPRINT",FACE,{"disambiguationData":[TD([[makeQuery(id+"F47.imprint","IMPRINT",EDGE,{"derivedFrom":sQuery(id+"F47.wireOp",EDGE,"E87.bottom")}),-1.0]])]});
            extrude(context, id + "F48", {"entities" : qUnion([Q0, Q1]), "operationType" : NewBodyOperationType.REMOVE, "oppositeDirection" : true, "depth" : 2.54 * mm, "offsetDistance" : 25.4 * mm});
        }
        {
            var Q0;
            {var subQ3=sQuery(id+"F6.wireOp",EDGE,"E12.top");var subQ8=sQuery(id+"F0.wireOp",EDGE,"E0.right");Q0=makeQuery(id+"F27.boolean.opBoolean","SPLIT",FACE,{"disambiguationData":[TD([makeQuery(id+"F7.opExtrude","SWEPT_FACE",FACE,{"disambiguationData":[OSD([subQ3])]})])],"derivedFrom":makeQuery(id+"F21.boolean.opBoolean","MERGE",FACE,{"derivedFrom":[makeQuery(id+"F7.boolean.opBoolean","MERGE",FACE,{"derivedFrom":[makeQuery(id+"F1.opExtrude","SWEPT_FACE",FACE,{"disambiguationData":[OSD([subQ8])]}),makeQuery(id+"F7.opExtrude","SWEPT_FACE",FACE,{"disambiguationData":[OSD([sQuery(id+"F6.wireOp",EDGE,"E10.right")])]}),makeQuery(id+"F7.opExtrude","SWEPT_FACE",FACE,{"disambiguationData":[OSD([sQuery(id+"F6.wireOp",EDGE,"E12.right")])]})]}),makeQuery(id+"F21.opExtrude","SWEPT_FACE",FACE,{"disambiguationData":[OSD([sQuery(id+"F20.wireOp",EDGE,"E33.right")])]}),makeQuery(id+"F21.opExtrude","SWEPT_FACE",FACE,{"disambiguationData":[OSD([sQuery(id+"F20.wireOp",EDGE,"E34.right")])]})]})});}
            var sketch = newSketch(context, id + "F49", { "sketchPlane" : qUnion([Q0])});
            skLineSegment(sketch, "E88.bottom", {"start": v(-5, 0) * mm, "end": v(5.03, 0) * mm});
            skLineSegment(sketch, "E88.top", {"start": v(-5, 19.13) * mm, "end": v(5.03, 19.13) * mm});
            skLineSegment(sketch, "E88.left", {"start": v(-5, 0) * mm, "end": v(-5, 19.13) * mm});
            skLineSegment(sketch, "E88.right", {"start": v(5.03, 0) * mm, "end": v(5.03, 19.13) * mm});
            skLineSegment(sketch, "E89.bottom", {"start": v(-39.53, 23.22) * mm, "end": v(-31.36, 23.22) * mm});
            skLineSegment(sketch, "E89.top", {"start": v(-39.53, 11.7) * mm, "end": v(-31.36, 11.7) * mm});
            skLineSegment(sketch, "E89.left", {"start": v(-39.53, 23.22) * mm, "end": v(-39.53, 11.7) * mm});
            skLineSegment(sketch, "E89.right", {"start": v(-31.36, 23.22) * mm, "end": v(-31.36, 11.7) * mm});
            skLineSegment(sketch, "E90.bottom", {"start": v(-23.75, 43.64) * mm, "end": v(-18, 43.64) * mm});
            skLineSegment(sketch, "E90.top", {"start": v(-23.75, 36.4) * mm, "end": v(-18, 36.4) * mm});
            skLineSegment(sketch, "E90.left", {"start": v(-23.75, 43.64) * mm, "end": v(-23.75, 36.4) * mm});
            skLineSegment(sketch, "E90.right", {"start": v(-18, 43.64) * mm, "end": v(-18, 36.4) * mm});
            skLineSegment(sketch, "E91.MirrorCS", {"start": v(23.75, 43.64) * mm, "end": v(18, 43.64) * mm});
            skLineSegment(sketch, "E92.MirrorCS", {"start": v(23.75, 43.64) * mm, "end": v(23.75, 36.4) * mm});
            skLineSegment(sketch, "E93.MirrorCS", {"start": v(23.75, 36.4) * mm, "end": v(18, 36.4) * mm});
            skLineSegment(sketch, "E94.MirrorCS", {"start": v(18, 43.64) * mm, "end": v(18, 36.4) * mm});
            skLineSegment(sketch, "E95.MirrorCS", {"start": v(31.36, 23.22) * mm, "end": v(31.36, 11.7) * mm});
            skLineSegment(sketch, "E96.MirrorCS", {"start": v(39.53, 23.22) * mm, "end": v(31.36, 23.22) * mm});
            skLineSegment(sketch, "E97.MirrorCS", {"start": v(39.53, 23.22) * mm, "end": v(39.53, 11.7) * mm});
            skLineSegment(sketch, "E98.MirrorCS", {"start": v(39.53, 11.7) * mm, "end": v(31.36, 11.7) * mm});
            skSolve(sketch);
        }
        {
            var Q0;
            Q0=makeQuery(id+"F49.imprint","IMPRINT",FACE,{"disambiguationData":[TD([[makeQuery(id+"F49.imprint","IMPRINT",EDGE,{"derivedFrom":sQuery(id+"F49.wireOp",EDGE,"E90.bottom")}),-1.0]])]});
            var Q1;
            Q1=makeQuery(id+"F49.imprint","IMPRINT",FACE,{"disambiguationData":[TD([[makeQuery(id+"F49.imprint","IMPRINT",EDGE,{"derivedFrom":sQuery(id+"F49.wireOp",EDGE,"E91.MirrorCS")}),1.0]])]});
            var Q2;
            Q2=makeQuery(id+"F49.imprint","IMPRINT",FACE,{"disambiguationData":[TD([[makeQuery(id+"F49.imprint","IMPRINT",EDGE,{"derivedFrom":sQuery(id+"F49.wireOp",EDGE,"E89.bottom")}),-1.0]])]});
            var Q3;
            Q3=makeQuery(id+"F49.imprint","IMPRINT",FACE,{"disambiguationData":[TD([[makeQuery(id+"F49.imprint","IMPRINT",EDGE,{"derivedFrom":sQuery(id+"F49.wireOp",EDGE,"E88.bottom")}),-1.0]])]});
            var Q4;
            Q4=makeQuery(id+"F49.imprint","IMPRINT",FACE,{"disambiguationData":[TD([[makeQuery(id+"F49.imprint","IMPRINT",EDGE,{"derivedFrom":sQuery(id+"F49.wireOp",EDGE,"E95.MirrorCS")}),1.0]])]});
            extrude(context, id + "F50", {"entities" : qUnion([Q0, Q1, Q2, Q3, Q4]), "operationType" : NewBodyOperationType.REMOVE, "oppositeDirection" : true, "depth" : 2.54 * mm, "offsetDistance" : 25.4 * mm});
        }
        {
            var Q0;
            {var subQ0=sQuery(id+"F6.wireOp",EDGE,"E12.top");var subQ5=sQuery(id+"F0.wireOp",EDGE,"E1.left");Q0=makeQuery(id+"F15.boolean.opBoolean","SPLIT",FACE,{"disambiguationData":[TD([makeQuery(id+"F7.opExtrude","SWEPT_FACE",FACE,{"disambiguationData":[OSD([subQ0])]})])],"derivedFrom":makeQuery(id+"F1.opExtrude","SWEPT_FACE",FACE,{"disambiguationData":[OSD([subQ5])]})});}
            var sketch = newSketch(context, id + "F51", { "sketchPlane" : qUnion([Q0])});
            skLineSegment(sketch, "E99", {"start": v(0, 275.57) * mm, "end": v(0, 0) * mm, "construction": true});
            skLineSegment(sketch, "E100.bottom", {"start": v(2.93, 58.28) * mm, "end": v(-2.93, 58.28) * mm});
            skLineSegment(sketch, "E100.top", {"start": v(2.93, 68.34) * mm, "end": v(-2.93, 68.34) * mm});
            skLineSegment(sketch, "E100.left", {"start": v(2.93, 58.28) * mm, "end": v(2.93, 68.34) * mm});
            skLineSegment(sketch, "E100.right", {"start": v(-2.93, 58.28) * mm, "end": v(-2.93, 68.34) * mm});
            skPoint(sketch, "E100.middle", {"position": v(0, 63.3) * mm});
            skLineSegment(sketch, "E101.0.1.0", {"start": v(2.93, 83.68) * mm, "end": v(-2.93, 83.68) * mm});
            skLineSegment(sketch, "E101.0.1.1", {"start": v(2.93, 93.74) * mm, "end": v(-2.93, 93.74) * mm});
            skLineSegment(sketch, "E101.0.1.2", {"start": v(2.93, 83.68) * mm, "end": v(2.93, 93.74) * mm});
            skLineSegment(sketch, "E101.0.1.3", {"start": v(-2.93, 83.68) * mm, "end": v(-2.93, 93.74) * mm});
            skLineSegment(sketch, "E101.0.2.0", {"start": v(2.93, 109.08) * mm, "end": v(-2.93, 109.08) * mm});
            skLineSegment(sketch, "E101.0.2.1", {"start": v(2.93, 119.14) * mm, "end": v(-2.93, 119.14) * mm});
            skLineSegment(sketch, "E101.0.2.2", {"start": v(2.93, 109.08) * mm, "end": v(2.93, 119.14) * mm});
            skLineSegment(sketch, "E101.0.2.3", {"start": v(-2.93, 109.08) * mm, "end": v(-2.93, 119.14) * mm});
            skLineSegment(sketch, "E101.0.3.0", {"start": v(2.93, 134.48) * mm, "end": v(-2.93, 134.48) * mm});
            skLineSegment(sketch, "E101.0.3.1", {"start": v(2.93, 144.54) * mm, "end": v(-2.93, 144.54) * mm});
            skLineSegment(sketch, "E101.0.3.2", {"start": v(2.93, 134.48) * mm, "end": v(2.93, 144.54) * mm});
            skLineSegment(sketch, "E101.0.3.3", {"start": v(-2.93, 134.48) * mm, "end": v(-2.93, 144.54) * mm});
            skLineSegment(sketch, "E101.0.4.0", {"start": v(2.93, 159.88) * mm, "end": v(-2.93, 159.88) * mm});
            skLineSegment(sketch, "E101.0.4.1", {"start": v(2.93, 169.94) * mm, "end": v(-2.93, 169.94) * mm});
            skLineSegment(sketch, "E101.0.4.2", {"start": v(2.93, 159.88) * mm, "end": v(2.93, 169.94) * mm});
            skLineSegment(sketch, "E101.0.4.3", {"start": v(-2.93, 159.88) * mm, "end": v(-2.93, 169.94) * mm});
            skLineSegment(sketch, "E101.0.5.0", {"start": v(2.93, 185.28) * mm, "end": v(-2.93, 185.28) * mm});
            skLineSegment(sketch, "E101.0.5.1", {"start": v(2.93, 195.34) * mm, "end": v(-2.93, 195.34) * mm});
            skLineSegment(sketch, "E101.0.5.2", {"start": v(2.93, 185.28) * mm, "end": v(2.93, 195.34) * mm});
            skLineSegment(sketch, "E101.0.5.3", {"start": v(-2.93, 185.28) * mm, "end": v(-2.93, 195.34) * mm});
            skLineSegment(sketch, "E101.0.6.0", {"start": v(2.93, 210.68) * mm, "end": v(-2.93, 210.68) * mm});
            skLineSegment(sketch, "E101.0.6.1", {"start": v(2.93, 220.74) * mm, "end": v(-2.93, 220.74) * mm});
            skLineSegment(sketch, "E101.0.6.2", {"start": v(2.93, 210.68) * mm, "end": v(2.93, 220.74) * mm});
            skLineSegment(sketch, "E101.0.6.3", {"start": v(-2.93, 210.68) * mm, "end": v(-2.93, 220.74) * mm});
            skLineSegment(sketch, "E101.direction1", {"start": v(-2.93, 58.28) * mm, "end": v(54.52, 57.68) * mm, "construction": true});
            skLineSegment(sketch, "E101.direction2", {"start": v(-2.93, 58.28) * mm, "end": v(-2.93, 83.68) * mm, "construction": true});
            skSolve(sketch);
        }
        {
            var Q0;
            Q0=makeQuery(id+"F51.imprint","IMPRINT",FACE,{"disambiguationData":[TD([[makeQuery(id+"F51.imprint","IMPRINT",EDGE,{"derivedFrom":sQuery(id+"F51.wireOp",EDGE,"E101.0.1.0")}),-1.0]])]});
            var Q1;
            Q1=makeQuery(id+"F51.imprint","IMPRINT",FACE,{"disambiguationData":[TD([[makeQuery(id+"F51.imprint","IMPRINT",EDGE,{"derivedFrom":sQuery(id+"F51.wireOp",EDGE,"E100.bottom")}),-1.0]])]});
            var Q2;
            Q2=makeQuery(id+"F51.imprint","IMPRINT",FACE,{"disambiguationData":[TD([[makeQuery(id+"F51.imprint","IMPRINT",EDGE,{"derivedFrom":sQuery(id+"F51.wireOp",EDGE,"E101.0.2.0")}),-1.0]])]});
            var Q3;
            Q3=makeQuery(id+"F51.imprint","IMPRINT",FACE,{"disambiguationData":[TD([[makeQuery(id+"F51.imprint","IMPRINT",EDGE,{"derivedFrom":sQuery(id+"F51.wireOp",EDGE,"E101.0.3.0")}),-1.0]])]});
            var Q4;
            Q4=makeQuery(id+"F51.imprint","IMPRINT",FACE,{"disambiguationData":[TD([[makeQuery(id+"F51.imprint","IMPRINT",EDGE,{"derivedFrom":sQuery(id+"F51.wireOp",EDGE,"E101.0.4.0")}),-1.0]])]});
            var Q5;
            Q5=makeQuery(id+"F51.imprint","IMPRINT",FACE,{"disambiguationData":[TD([[makeQuery(id+"F51.imprint","IMPRINT",EDGE,{"derivedFrom":sQuery(id+"F51.wireOp",EDGE,"E101.0.5.0")}),-1.0]])]});
            var Q6;
            Q6=makeQuery(id+"F51.imprint","IMPRINT",FACE,{"disambiguationData":[TD([[makeQuery(id+"F51.imprint","IMPRINT",EDGE,{"derivedFrom":sQuery(id+"F51.wireOp",EDGE,"E101.0.6.0")}),-1.0]])]});
            extrude(context, id + "F52", {"entities" : qUnion([Q0, Q1, Q2, Q3, Q4, Q5, Q6]), "operationType" : NewBodyOperationType.REMOVE, "oppositeDirection" : true, "depth" : 25.4 * mm, "offsetDistance" : 25.4 * mm});
        }
        {
            var Q0;
            Q0=qCreatedBy(makeId("Right.planeOp"),FACE);
            var sketch = newSketch(context, id + "F53", { "sketchPlane" : qUnion([Q0])});
            skLineSegment(sketch, "E102.bottom", {"start": v(2.62, 50.84) * mm, "end": v(-2.5, 50.84) * mm});
            skLineSegment(sketch, "E102.top", {"start": v(2.62, 59.11) * mm, "end": v(-2.5, 59.11) * mm});
            skLineSegment(sketch, "E102.left", {"start": v(2.62, 50.84) * mm, "end": v(2.62, 59.11) * mm});
            skLineSegment(sketch, "E102.right", {"start": v(-2.5, 50.84) * mm, "end": v(-2.5, 59.11) * mm});
            skSolve(sketch);
        }
        {
            var Q0;
            Q0=makeQuery(id+"F53.imprint","IMPRINT",FACE,{"disambiguationData":[TD([[makeQuery(id+"F53.imprint","IMPRINT",EDGE,{"derivedFrom":sQuery(id+"F53.wireOp",EDGE,"E102.bottom")}),-1.0]])]});
            extrude(context, id + "F54", {"entities" : qUnion([Q0]), "operationType" : NewBodyOperationType.REMOVE, "depth" : 15.24 * mm, "offsetDistance" : 25.4 * mm});
        }
    });
